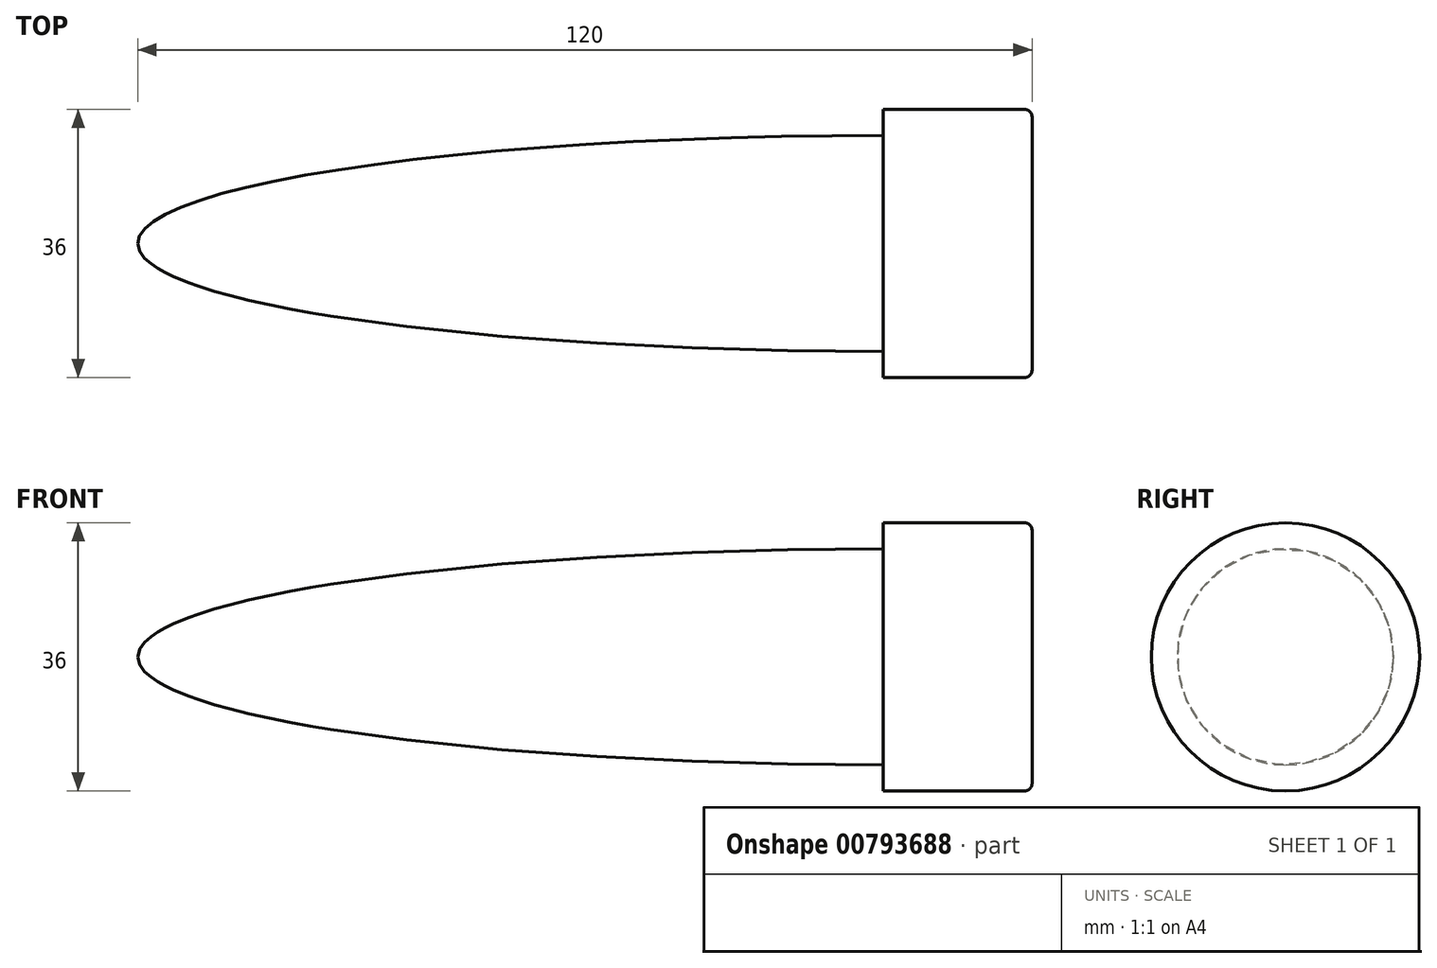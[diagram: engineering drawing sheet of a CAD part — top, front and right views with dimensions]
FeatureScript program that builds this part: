
annotation { "Feature Type Name" : "Feature", "Feature Type Description" : "" }
export const myFeature = defineFeature(function(context is Context, id is Id, definition is map)
    precondition{}
    {
        {
            var Q0;
            Q0=qCreatedBy(makeId("Top.planeOp"),FACE);
            var sketch = newSketch(context, id + "F0", { "sketchPlane" : qUnion([Q0])});
            skLineSegment(sketch, "E0", {"start": v(100, 0) * mm, "end": v(-49.92, 0) * mm, "construction": true});
            skLineSegment(sketch, "E1", {"start": v(0, 0) * mm, "end": v(0, 19) * mm, "construction": true});
            skLineSegment(sketch, "E2", {"start": v(100, 0) * mm, "end": v(100, 19) * mm, "construction": true});
            skLineSegment(sketch, "E3", {"start": v(-37.94, 19) * mm, "end": v(100, 19) * mm, "construction": true});
            skLineSegment(sketch, "E4.bottom", {"start": v(100, 18) * mm, "end": v(119, 18) * mm});
            skLineSegment(sketch, "E4.right", {"start": v(120, 17) * mm, "end": v(120, 0) * mm});
            skLineSegment(sketch, "E5", {"start": v(100, 19) * mm, "end": v(100, 18) * mm});
            skLineSegment(sketch, "E6", {"start": v(0, 0) * mm, "end": v(120, 0) * mm});
            skLineSegment(sketch, "E7.left", {"start": v(100, 19) * mm, "end": v(100, 19) * mm});
            skLineSegment(sketch, "E8.bottom", {"start": v(0, 0) * mm, "end": v(115, 0) * mm});
            skLineSegment(sketch, "E8.left", {"start": v(0, 0) * mm, "end": v(0, 14.5) * mm});
            skPoint(sketch, "E9.visualSharp", {"position": v(120, 18) * mm});
            skArc(sketch, "E9.filletArc", {"start": v(120, 17) * mm, "mid": v(119.7, 17.7) * mm, "end": v(119, 18) * mm});
            skSolve(sketch);
        }
        {
            var Q0;
            Q0=qCreatedBy(makeId("Top.planeOp"),FACE);
            var sketch = newSketch(context, id + "F1", { "sketchPlane" : qUnion([Q0])});
            skLineSegment(sketch, "E10.0", {"start": v(100, 0) * mm, "end": v(-49.92, 0) * mm});
            skLineSegment(sketch, "E10.1", {"start": v(0, 0) * mm, "end": v(0, 19) * mm});
            skLineSegment(sketch, "E10.2", {"start": v(100, 0) * mm, "end": v(100, 19) * mm});
            skLineSegment(sketch, "E10.4", {"start": v(100, 18) * mm, "end": v(119, 18) * mm});
            skLineSegment(sketch, "E10.5", {"start": v(120, 17) * mm, "end": v(120, 0) * mm});
            skLineSegment(sketch, "E10.6", {"start": v(100, 19) * mm, "end": v(100, 18) * mm});
            skLineSegment(sketch, "E10.7", {"start": v(0, 0) * mm, "end": v(120, 0) * mm});
            skPoint(sketch, "E10.8", {"position": v(100, 19) * mm});
            skLineSegment(sketch, "E10.9", {"start": v(0, 0) * mm, "end": v(115, 0) * mm});
            skLineSegment(sketch, "E10.10", {"start": v(0, 0) * mm, "end": v(0, 14.5) * mm});
            skPoint(sketch, "E11.11", {"position": v(120, 18) * mm});
            skArc(sketch, "E11.12", {"start": v(120, 17) * mm, "mid": v(119.7, 17.7) * mm, "end": v(119, 18) * mm});
            skLineSegment(sketch, "E12", {"start": v(100, 19) * mm, "end": v(-17.29, 19) * mm, "construction": true});
            skEllipse(sketch, "E13", {"center": v(100, 0) * mm, "majorRadius": 100 * mm, "minorRadius": 14.5 * mm, "majorAxis": v(-1, 0)});
            skSolve(sketch);
        }
        {
            var Q0;
            {var subQ0=sQuery(id+"F1.wireOp",EDGE,"E10.2");Q0=makeQuery(id+"F1.imprint","IMPRINT",FACE,{"disambiguationData":[TD([[makeQuery(id+"F1.imprint","IMPRINT",EDGE,{"derivedFrom":subQ0}),1.0]])]});}
            var Q1;
            {var subQ2=sQuery(id+"F1.wireOp",EDGE,"E10.2");Q1=makeQuery(id+"F1.imprint","IMPRINT",FACE,{"disambiguationData":[TD([[makeQuery(id+"F1.imprint","IMPRINT",EDGE,{"derivedFrom":subQ2}),-1.0]])]});}
            var Q2;
            Q2=sQuery(id+"F1.wireOp",EDGE,"E10.0");
            revolve(context, id + "F2", {"surfaceOperationType" : NewSurfaceOperationType.NEW, "entities" : qUnion([Q0, Q1]), "axis" : qUnion([Q2]), "revolveType" : RevolveType.FULL});
        }
    });
